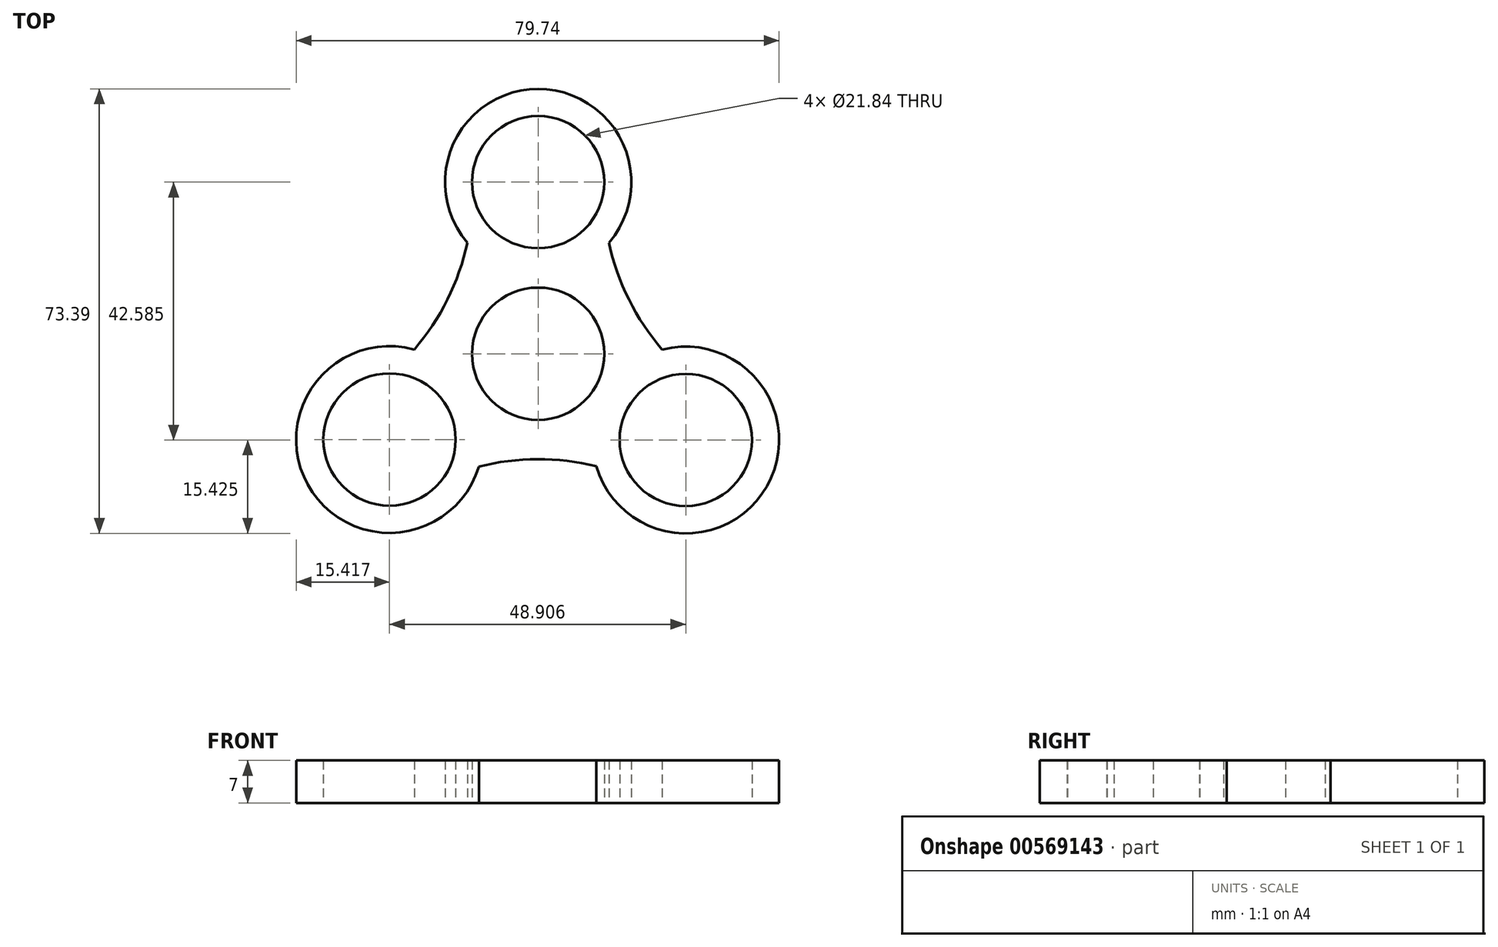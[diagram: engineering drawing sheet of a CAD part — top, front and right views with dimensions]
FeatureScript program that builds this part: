
annotation { "Feature Type Name" : "Feature", "Feature Type Description" : "" }
export const myFeature = defineFeature(function(context is Context, id is Id, definition is map)
    precondition{}
    {
        {
            var Q0;
            Q0=qCreatedBy(makeId("Top.planeOp"),FACE);
            var sketch = newSketch(context, id + "F0", { "sketchPlane" : qUnion([Q0])});
            skCircle(sketch, "E0", {"center": v(0, 0) * mm, "radius": 10.92 * mm});
            skCircle(sketch, "E1.1.0", {"center": v(24.36, -14.25) * mm, "radius": 10.92 * mm});
            skCircle(sketch, "E1.2.0", {"center": v(-24.54, -14.17) * mm, "radius": 10.92 * mm});
            skPoint(sketch, "E1.center", {"position": v(-0.07, 0) * mm});
            skArc(sketch, "E2", {"start": v(9.57, -18.58) * mm, "mid": v(-0.11, -17.42) * mm, "end": v(-9.78, -18.63) * mm});
            skArc(sketch, "E3", {"start": v(10.82, 28.34) * mm, "mid": v(10.8, 28) * mm, "end": v(10.8, 27.64) * mm});
            skArc(sketch, "E4", {"start": v(-20.47, 0.7) * mm, "mid": v(-14.97, 8.98) * mm, "end": v(-11.69, 18.35) * mm});
            skArc(sketch, "E5", {"start": v(11.69, 18.35) * mm, "mid": v(0, 43.72) * mm, "end": v(-11.69, 18.35) * mm});
            skArc(sketch, "E6", {"start": v(-20.47, 0.7) * mm, "mid": v(-38.04, -21.63) * mm, "end": v(-9.78, -18.63) * mm});
            skArc(sketch, "E7", {"start": v(9.57, -18.58) * mm, "mid": v(37.78, -21.85) * mm, "end": v(20.49, 0.68) * mm});
            skArc(sketch, "E8.trimOffspring", {"start": v(-10.8, 27.64) * mm, "mid": v(-10.8, 27.96) * mm, "end": v(-10.82, 28.28) * mm});
            skArc(sketch, "E9.trimOffspring", {"start": v(11.69, 18.35) * mm, "mid": v(14.98, 8.96) * mm, "end": v(20.49, 0.68) * mm});
            skCircle(sketch, "E10", {"center": v(0, 28.34) * mm, "radius": 10.92 * mm});
            skSolve(sketch);
        }
        {
            var Q0;
            Q0 = qSketchRegion(id + "F0", true);
            extrude(context, id + "F1", {"entities" : qUnion([Q0]), "depth" : 7 * mm, "offsetDistance" : 25 * mm});
        }
    });
